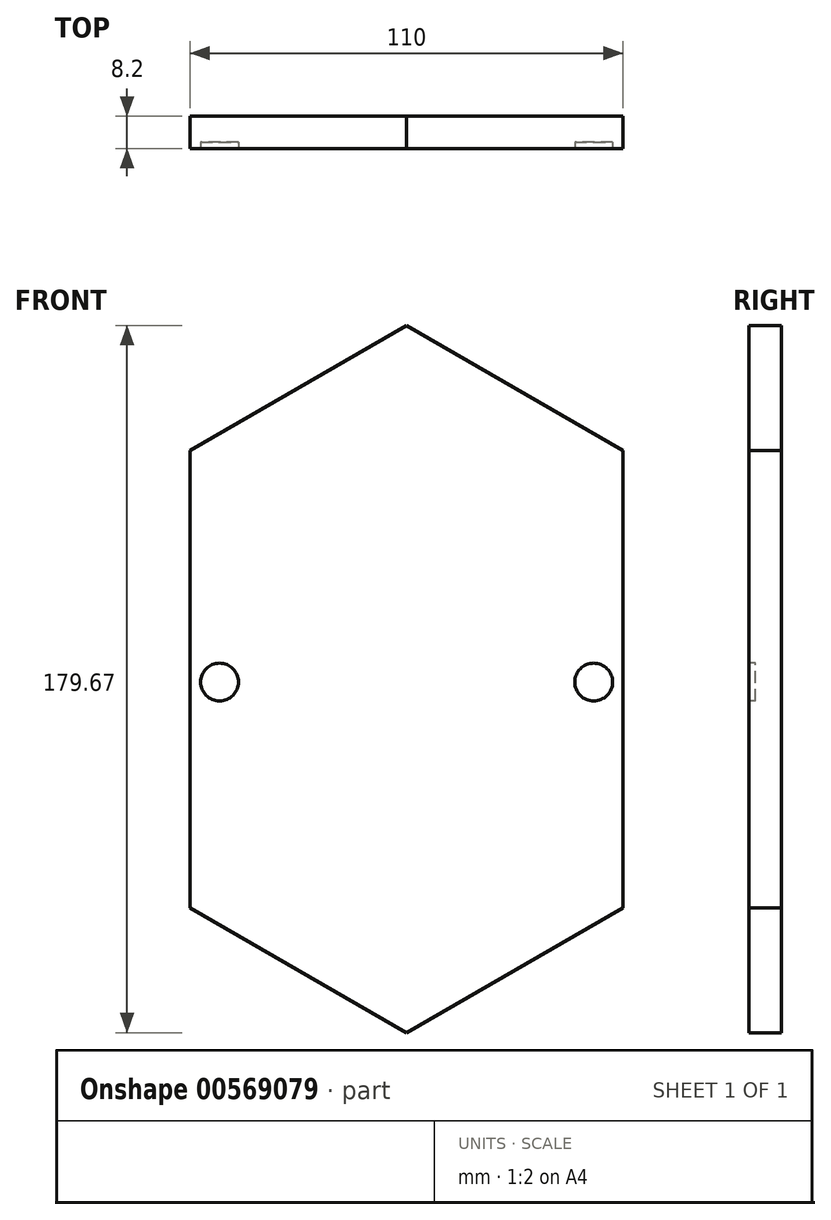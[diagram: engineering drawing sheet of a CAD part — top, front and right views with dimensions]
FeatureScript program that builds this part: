
annotation { "Feature Type Name" : "Feature", "Feature Type Description" : "" }
export const myFeature = defineFeature(function(context is Context, id is Id, definition is map)
    precondition{}
    {
        {
            var Q0;
            Q0=qCreatedBy(makeId("Front.planeOp"),FACE);
            var sketch = newSketch(context, id + "F0", { "sketchPlane" : qUnion([Q0])});
            skLineSegment(sketch, "E0", {"start": v(0, 0) * mm, "end": v(-55, 31.75) * mm});
            skLineSegment(sketch, "E1", {"start": v(-55, 31.75) * mm, "end": v(-55, 147.91) * mm});
            skLineSegment(sketch, "E2", {"start": v(-55, 147.91) * mm, "end": v(0, 179.67) * mm});
            skLineSegment(sketch, "E3", {"start": v(0, 179.67) * mm, "end": v(55, 147.91) * mm});
            skLineSegment(sketch, "E4", {"start": v(55, 147.91) * mm, "end": v(55, 31.75) * mm});
            skLineSegment(sketch, "E5", {"start": v(55, 31.75) * mm, "end": v(0, 0) * mm});
            skSolve(sketch);
        }
        {
            var Q0;
            Q0 = qSketchRegion(id + "F0", true);
            extrude(context, id + "F1", {"entities" : qUnion([Q0]), "endBound" : BoundingType.SYMMETRIC, "depth" : 0.2 * mm, "offsetDistance" : 25 * mm});
        }
        {
            var Q0;
            Q0=makeQuery(id+"F1.opExtrude","CAP_FACE",FACE,{"disambiguationData":[OSD([sQuery(id+"F0.wireOp",EDGE,"E0"),sQuery(id+"F0.wireOp",EDGE,"E1"),sQuery(id+"F0.wireOp",EDGE,"E2"),sQuery(id+"F0.wireOp",EDGE,"E3"),sQuery(id+"F0.wireOp",EDGE,"E4"),sQuery(id+"F0.wireOp",EDGE,"E5")])],"isStart":false});
            var sketch = newSketch(context, id + "F2", { "sketchPlane" : qUnion([Q0])});
            skLineSegment(sketch, "E6.0", {"start": v(-55, 147.91) * mm, "end": v(0, 179.67) * mm});
            skLineSegment(sketch, "E6.1", {"start": v(0, 179.67) * mm, "end": v(55, 147.91) * mm});
            skLineSegment(sketch, "E6.2", {"start": v(55, 147.91) * mm, "end": v(55, 31.75) * mm});
            skLineSegment(sketch, "E6.3", {"start": v(55, 31.75) * mm, "end": v(0, 0) * mm});
            skLineSegment(sketch, "E6.4", {"start": v(0, 0) * mm, "end": v(-55, 31.75) * mm});
            skLineSegment(sketch, "E6.5", {"start": v(-55, 31.75) * mm, "end": v(-55, 147.91) * mm});
            skSolve(sketch);
        }
        {
            var Q0;
            Q0 = qSketchRegion(id + "F2", true);
            extrude(context, id + "F3", {"entities" : qUnion([Q0]), "depth" : 4 * mm, "offsetDistance" : 25 * mm});
        }
        {
            var Q0;
            Q0=makeQuery(id+"F3.opExtrude","CAP_FACE",FACE,{"disambiguationData":[OSD([sQuery(id+"F2.wireOp",EDGE,"E6.0"),sQuery(id+"F2.wireOp",EDGE,"E6.1"),sQuery(id+"F2.wireOp",EDGE,"E6.2"),sQuery(id+"F2.wireOp",EDGE,"E6.3"),sQuery(id+"F2.wireOp",EDGE,"E6.4"),sQuery(id+"F2.wireOp",EDGE,"E6.5")])],"isStart":false});
            var sketch = newSketch(context, id + "F4", { "sketchPlane" : qUnion([Q0])});
            skLineSegment(sketch, "E7", {"start": v(55, 89.83) * mm, "end": v(-55, 89.83) * mm, "construction": true});
            skCircle(sketch, "E8", {"center": v(62, 89.83) * mm, "radius": 4.8 * mm});
            skCircle(sketch, "E9", {"center": v(-62, 89.83) * mm, "radius": 4.8 * mm});
            skSolve(sketch);
        }
        {
            var Q0;
            Q0 = qSketchRegion(id + "F4", true);
            extrude(context, id + "F5", {"entities" : qUnion([Q0]), "operationType" : NewBodyOperationType.REMOVE, "oppositeDirection" : true, "depth" : 1.6 * mm, "offsetDistance" : 25 * mm});
        }
        {
            var Q0;
            Q0=makeQuery(id+"F3.opExtrude","SWEPT_BODY",BODY,{"disambiguationData":[OSD([sQuery(id+"F2.wireOp",EDGE,"E6.0"),sQuery(id+"F2.wireOp",EDGE,"E6.1"),sQuery(id+"F2.wireOp",EDGE,"E6.2"),sQuery(id+"F2.wireOp",EDGE,"E6.3"),sQuery(id+"F2.wireOp",EDGE,"E6.4"),sQuery(id+"F2.wireOp",EDGE,"E6.5")])]});
            var Q1;
            Q1=makeQuery(id+"F8.opExtrude","SWEPT_BODY",BODY,{"disambiguationData":[OSD([sQuery(id+"F7.wireOp",EDGE,"E10.0")])]});
            var Q2;
            Q2=makeQuery(id+"F8.opExtrude","SWEPT_BODY",BODY,{"disambiguationData":[OSD([sQuery(id+"F7.wireOp",EDGE,"E10.1")])]});
            var Q3;
            Q3=qCreatedBy(makeId("Front.planeOp"),FACE);
            mirror(context, id + "F6", {"operationType" : NewBodyOperationType.ADD, "entities" : qUnion([Q0, Q1, Q2]), "mirrorPlane" : qUnion([Q3])});
        }
        {
            var Q0;
            Q0=makeQuery(id+"F3.opExtrude","CAP_FACE",FACE,{"disambiguationData":[OSD([sQuery(id+"F2.wireOp",EDGE,"E6.0"),sQuery(id+"F2.wireOp",EDGE,"E6.1"),sQuery(id+"F2.wireOp",EDGE,"E6.2"),sQuery(id+"F2.wireOp",EDGE,"E6.3"),sQuery(id+"F2.wireOp",EDGE,"E6.4"),sQuery(id+"F2.wireOp",EDGE,"E6.5")])],"isStart":false});
            var sketch = newSketch(context, id + "F7", { "sketchPlane" : qUnion([Q0])});
            skCircle(sketch, "E10.0", {"center": v(-47.53, 89.07) * mm, "radius": 4.8 * mm});
            skCircle(sketch, "E10.1", {"center": v(47.53, 89.07) * mm, "radius": 4.8 * mm});
            skSolve(sketch);
        }
        {
            var Q0;
            Q0 = qSketchRegion(id + "F7", true);
            extrude(context, id + "F8", {"entities" : qUnion([Q0]), "oppositeDirection" : true, "depth" : 1.6 * mm, "offsetDistance" : 25 * mm});
        }
    });
